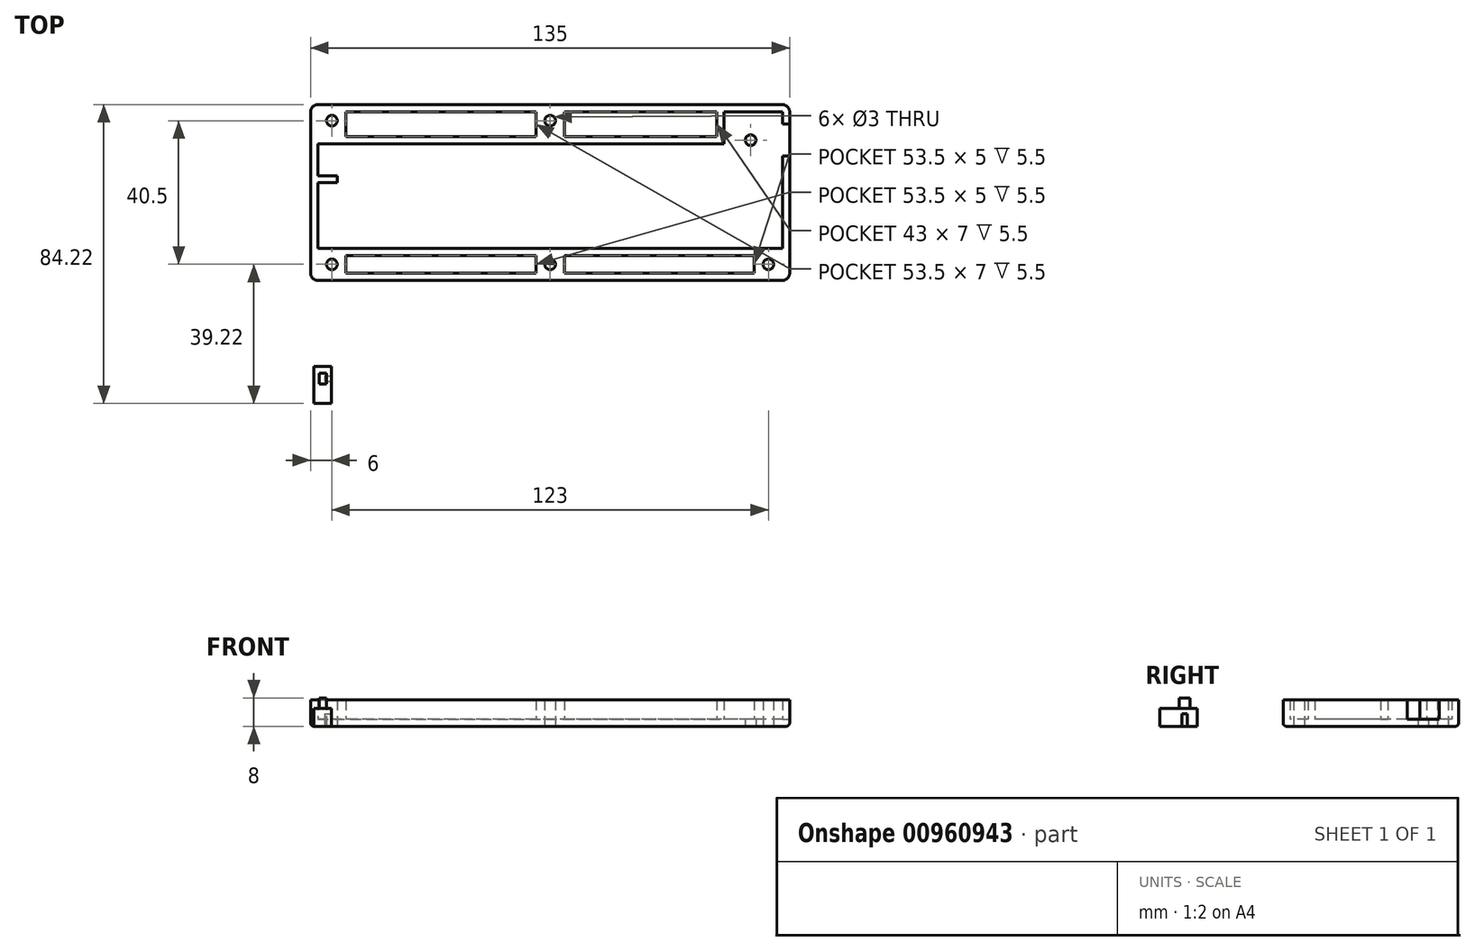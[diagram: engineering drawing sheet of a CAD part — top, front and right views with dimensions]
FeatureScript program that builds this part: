
annotation { "Feature Type Name" : "Feature", "Feature Type Description" : "" }
export const myFeature = defineFeature(function(context is Context, id is Id, definition is map)
    precondition{}
    {
        {
            var Q0;
            Q0=qCreatedBy(makeId("Top.planeOp"),FACE);
            var sketch = newSketch(context, id + "F0", { "sketchPlane" : qUnion([Q0])});
            skLineSegment(sketch, "E0.bottom", {"start": v(65.5, 19.25) * mm, "end": v(-65.5, 19.25) * mm});
            skLineSegment(sketch, "E0.top", {"start": v(65.5, -19.25) * mm, "end": v(-65.5, -19.25) * mm});
            skLineSegment(sketch, "E0.left", {"start": v(65.5, 19.25) * mm, "end": v(65.5, -19.25) * mm});
            skLineSegment(sketch, "E0.right", {"start": v(-65.5, 19.25) * mm, "end": v(-65.5, -19.25) * mm});
            skPoint(sketch, "E0.middle", {"position": v(0, 0) * mm});
            skPoint(sketch, "E1", {"position": v(49, 19.25) * mm});
            skPoint(sketch, "E2", {"position": v(-65.5, 10.25) * mm});
            skLineSegment(sketch, "E3", {"start": v(-65.5, 10.25) * mm, "end": v(49, 10.25) * mm});
            skLineSegment(sketch, "E4", {"start": v(49, 10.25) * mm, "end": v(49, 19.25) * mm});
            skPoint(sketch, "E5", {"position": v(-60, -19.25) * mm});
            skLineSegment(sketch, "E6", {"start": v(-60, -19.25) * mm, "end": v(-60, 10.25) * mm});
            skLineSegment(sketch, "E7.0", {"start": v(67.5, 21.25) * mm, "end": v(-67.5, 21.25) * mm});
            skLineSegment(sketch, "E7.1", {"start": v(67.5, 21.25) * mm, "end": v(67.5, -21.25) * mm});
            skLineSegment(sketch, "E7.2", {"start": v(67.5, -21.25) * mm, "end": v(-67.5, -21.25) * mm});
            skLineSegment(sketch, "E7.3", {"start": v(-67.5, 21.25) * mm, "end": v(-67.5, -21.25) * mm});
            skPoint(sketch, "E8", {"position": v(65.5, 15.75) * mm});
            skPoint(sketch, "E9", {"position": v(65.5, 6.75) * mm});
            skLineSegment(sketch, "E10.0", {"start": v(47, 12.25) * mm, "end": v(47, 19.25) * mm});
            skLineSegment(sketch, "E10.1", {"start": v(-65.5, 12.25) * mm, "end": v(47, 12.25) * mm});
            skPoint(sketch, "E11", {"position": v(-65.5, 1.25) * mm});
            skLineSegment(sketch, "E12", {"start": v(-65.5, 1.25) * mm, "end": v(-60, 1.25) * mm});
            skLineSegment(sketch, "E13.0", {"start": v(-65.5, -0.75) * mm, "end": v(-60, -0.75) * mm});
            skLineSegment(sketch, "E14", {"start": v(47, 19.25) * mm, "end": v(47, 21.25) * mm});
            skLineSegment(sketch, "E15", {"start": v(-65.5, 12.25) * mm, "end": v(-67.5, 12.25) * mm});
            skLineSegment(sketch, "E16", {"start": v(-65.5, 10.25) * mm, "end": v(-67.5, 10.25) * mm});
            skLineSegment(sketch, "E17", {"start": v(-65.5, 1.25) * mm, "end": v(-67.5, 1.25) * mm});
            skLineSegment(sketch, "E18", {"start": v(-65.5, -0.75) * mm, "end": v(-67.5, -0.75) * mm});
            skLineSegment(sketch, "E19", {"start": v(65.5, 15.75) * mm, "end": v(67.5, 15.75) * mm});
            skLineSegment(sketch, "E20", {"start": v(65.5, 6.75) * mm, "end": v(67.5, 6.75) * mm});
            skPoint(sketch, "E21", {"position": v(0, -19.25) * mm});
            skPoint(sketch, "E22", {"position": v(0, -4.25) * mm});
            skLineSegment(sketch, "E23.bottom", {"start": v(24, -13.25) * mm, "end": v(-24, -13.25) * mm});
            skLineSegment(sketch, "E23.top", {"start": v(24, 4.75) * mm, "end": v(-24, 4.75) * mm});
            skLineSegment(sketch, "E23.left", {"start": v(24, -13.25) * mm, "end": v(24, 4.75) * mm});
            skLineSegment(sketch, "E23.right", {"start": v(-24, -13.25) * mm, "end": v(-24, 4.75) * mm});
            skLineSegment(sketch, "E24.0", {"start": v(26, -15.25) * mm, "end": v(26, 6.75) * mm});
            skLineSegment(sketch, "E24.1", {"start": v(26, -15.25) * mm, "end": v(-26, -15.25) * mm});
            skLineSegment(sketch, "E24.2", {"start": v(-26, -15.25) * mm, "end": v(-26, 6.75) * mm});
            skLineSegment(sketch, "E24.3", {"start": v(26, 6.75) * mm, "end": v(-26, 6.75) * mm});
            skPoint(sketch, "E25", {"position": v(-67.5, -28.25) * mm});
            skLineSegment(sketch, "E26.bottom", {"start": v(-67.5, -28.25) * mm, "end": v(67.5, -28.25) * mm});
            skLineSegment(sketch, "E26.top", {"start": v(-67.5, -21.25) * mm, "end": v(67.5, -21.25) * mm});
            skLineSegment(sketch, "E26.left", {"start": v(-67.5, -28.25) * mm, "end": v(-67.5, -21.25) * mm});
            skLineSegment(sketch, "E26.right", {"start": v(67.5, -28.25) * mm, "end": v(67.5, -21.25) * mm});
            skPoint(sketch, "E27", {"position": v(-67.5, 16.75) * mm});
            skLineSegment(sketch, "E28", {"start": v(-67.5, 16.75) * mm, "end": v(47, 16.75) * mm, "construction": true});
            skPoint(sketch, "E29", {"position": v(-67.5, -23.75) * mm});
            skLineSegment(sketch, "E30", {"start": v(-67.5, -23.75) * mm, "end": v(67.5, -23.75) * mm, "construction": true});
            skPoint(sketch, "E31", {"position": v(-61.5, 16.75) * mm});
            skPoint(sketch, "E32", {"position": v(-61.5, -23.75) * mm});
            skPoint(sketch, "E33", {"position": v(61.5, -23.75) * mm});
            skPoint(sketch, "E34", {"position": v(0, -23.75) * mm});
            skPoint(sketch, "E35", {"position": v(0, 16.75) * mm});
            skPoint(sketch, "E36", {"position": v(65.5, 11.25) * mm});
            skPoint(sketch, "E37", {"position": v(56.5, 11.25) * mm});
            skCircle(sketch, "E38", {"center": v(56.5, 11.25) * mm, "radius": 1.5 * mm});
            skCircle(sketch, "E39", {"center": v(0, 16.75) * mm, "radius": 1.5 * mm});
            skCircle(sketch, "E40", {"center": v(-61.5, 16.75) * mm, "radius": 1.5 * mm});
            skCircle(sketch, "E41", {"center": v(-61.5, -23.75) * mm, "radius": 1.5 * mm});
            skCircle(sketch, "E42", {"center": v(0, -23.75) * mm, "radius": 1.5 * mm});
            skCircle(sketch, "E43", {"center": v(61.5, -23.75) * mm, "radius": 1.5 * mm});
            skPoint(sketch, "E44", {"position": v(-57.5, 21.25) * mm});
            skLineSegment(sketch, "E45", {"start": v(-57.5, 21.25) * mm, "end": v(-57.5, 12.25) * mm});
            skLineSegment(sketch, "E46.bottom", {"start": v(4, 12.25) * mm, "end": v(-4, 12.25) * mm});
            skLineSegment(sketch, "E46.top", {"start": v(4, 21.25) * mm, "end": v(-4, 21.25) * mm});
            skLineSegment(sketch, "E46.left", {"start": v(4, 12.25) * mm, "end": v(4, 21.25) * mm});
            skLineSegment(sketch, "E46.right", {"start": v(-4, 12.25) * mm, "end": v(-4, 21.25) * mm});
            skLineSegment(sketch, "E47", {"start": v(-57.5, -21.25) * mm, "end": v(-57.5, -28.25) * mm});
            skLineSegment(sketch, "E48.bottom", {"start": v(4, -19.25) * mm, "end": v(-4, -19.25) * mm});
            skLineSegment(sketch, "E48.top", {"start": v(4, -28.25) * mm, "end": v(-4, -28.25) * mm});
            skLineSegment(sketch, "E48.left", {"start": v(4, -19.25) * mm, "end": v(4, -28.25) * mm});
            skLineSegment(sketch, "E48.right", {"start": v(-4, -19.25) * mm, "end": v(-4, -28.25) * mm});
            skLineSegment(sketch, "E49", {"start": v(57.5, -28.25) * mm, "end": v(57.5, -19.25) * mm});
            skPoint(sketch, "E50", {"position": v(-67.5, -26.25) * mm});
            skLineSegment(sketch, "E51", {"start": v(-67.5, -26.25) * mm, "end": v(67.5, -26.25) * mm});
            skSolve(sketch);
        }
        {
            var Q0;
            {var subQ0=sQuery(id+"F0.wireOp",EDGE,"E4");Q0=makeQuery(id+"F0.imprint","IMPRINT",FACE,{"disambiguationData":[TD([[makeQuery(id+"F0.imprint","IMPRINT",EDGE,{"derivedFrom":subQ0}),-1.0]])]});}
            var Q1;
            {var subQ3=sQuery(id+"F0.wireOp",EDGE,"E12");Q1=makeQuery(id+"F0.imprint","IMPRINT",FACE,{"disambiguationData":[TD([[makeQuery(id+"F0.imprint","IMPRINT",EDGE,{"derivedFrom":subQ3}),1.0]])]});}
            var Q2;
            {var subQ5=sQuery(id+"F0.wireOp",EDGE,"E13.0");Q2=makeQuery(id+"F0.imprint","IMPRINT",FACE,{"disambiguationData":[TD([[makeQuery(id+"F0.imprint","IMPRINT",EDGE,{"derivedFrom":subQ5}),-1.0]])]});}
            var Q3;
            {var subQ2=sQuery(id+"F0.wireOp",EDGE,"E19");Q3=makeQuery(id+"F0.imprint","IMPRINT",FACE,{"disambiguationData":[TD([[makeQuery(id+"F0.imprint","IMPRINT",EDGE,{"derivedFrom":subQ2}),-1.0]])]});}
            var Q4;
            Q4=makeQuery(id+"F0.imprint","IMPRINT",FACE,{"disambiguationData":[TD([[makeQuery(id+"F0.imprint","IMPRINT",EDGE,{"derivedFrom":sQuery(id+"F0.wireOp",EDGE,"E23.bottom")}),1.0]])]});
            var Q5;
            {var subQ0=sQuery(id+"F0.wireOp",EDGE,"E46.right");var subQ1=sQuery(id+"F0.wireOp",EDGE,"E0.bottom");var subQ2=makeQuery(id+"F0.imprint","INTERSECT",VERTEX,{"derivedFrom":[subQ1,subQ0]});Q5=makeQuery(id+"F0.imprint","IMPRINT",FACE,{"disambiguationData":[TD([[makeQuery(id+"F0.imprint","IMPRINT",EDGE,{"disambiguationData":[TD([[subQ2,-1.0]])],"derivedFrom":subQ1}),1.0]])]});}
            var Q6;
            {var subQ0=sQuery(id+"F0.wireOp",EDGE,"E10.0");Q6=makeQuery(id+"F0.imprint","IMPRINT",FACE,{"disambiguationData":[TD([[makeQuery(id+"F0.imprint","IMPRINT",EDGE,{"derivedFrom":subQ0}),1.0]])]});}
            var Q7;
            {var subQ0=sQuery(id+"F0.wireOp",EDGE,"E49");var subQ1=sQuery(id+"F0.wireOp",EDGE,"E7.2");var subQ2=makeQuery(id+"F0.imprint","INTERSECT",VERTEX,{"derivedFrom":[subQ1,subQ0]});Q7=makeQuery(id+"F0.imprint","IMPRINT",FACE,{"disambiguationData":[TD([[makeQuery(id+"F0.imprint","IMPRINT",EDGE,{"disambiguationData":[TD([[subQ2,-1.0]])],"derivedFrom":subQ1}),1.0]])]});}
            var Q8;
            {var subQ0=sQuery(id+"F0.wireOp",EDGE,"E48.right");var subQ1=sQuery(id+"F0.wireOp",EDGE,"E7.2");var subQ2=makeQuery(id+"F0.imprint","INTERSECT",VERTEX,{"derivedFrom":[subQ1,subQ0]});Q8=makeQuery(id+"F0.imprint","IMPRINT",FACE,{"disambiguationData":[TD([[makeQuery(id+"F0.imprint","IMPRINT",EDGE,{"disambiguationData":[TD([[subQ2,-1.0]])],"derivedFrom":subQ1}),1.0]])]});}
            extrude(context, id + "F1", {"entities" : qUnion([Q0, Q1, Q2, Q3, Q4, Q5, Q6, Q7, Q8]), "depth" : 2 * mm, "offsetDistance" : 25 * mm});
        }
        {
            var Q0;
            {var subQ2=sQuery(id+"F0.wireOp",EDGE,"E4");Q0=makeQuery(id+"F0.imprint","IMPRINT",FACE,{"disambiguationData":[TD([[makeQuery(id+"F0.imprint","IMPRINT",EDGE,{"derivedFrom":subQ2}),1.0]])]});}
            var Q1;
            {var subQ2=sQuery(id+"F0.wireOp",EDGE,"E15");Q1=makeQuery(id+"F0.imprint","IMPRINT",FACE,{"disambiguationData":[TD([[makeQuery(id+"F0.imprint","IMPRINT",EDGE,{"derivedFrom":subQ2}),1.0]])]});}
            var Q2;
            {var subQ0=sQuery(id+"F0.wireOp",EDGE,"E16");Q2=makeQuery(id+"F0.imprint","IMPRINT",FACE,{"disambiguationData":[TD([[makeQuery(id+"F0.imprint","IMPRINT",EDGE,{"derivedFrom":subQ0}),1.0]])]});}
            var Q3;
            {var subQ2=sQuery(id+"F0.wireOp",EDGE,"E17");Q3=makeQuery(id+"F0.imprint","IMPRINT",FACE,{"disambiguationData":[TD([[makeQuery(id+"F0.imprint","IMPRINT",EDGE,{"derivedFrom":subQ2}),1.0]])]});}
            var Q4;
            {var subQ2=sQuery(id+"F0.wireOp",EDGE,"E12");Q4=makeQuery(id+"F0.imprint","IMPRINT",FACE,{"disambiguationData":[TD([[makeQuery(id+"F0.imprint","IMPRINT",EDGE,{"derivedFrom":subQ2}),-1.0]])]});}
            var Q5;
            {var subQ4=sQuery(id+"F0.wireOp",EDGE,"E7.2");Q5=makeQuery(id+"F0.imprint","IMPRINT",FACE,{"disambiguationData":[TD([[makeQuery(id+"F0.imprint","IMPRINT",EDGE,{"derivedFrom":subQ4}),-1.0]])]});}
            var Q6;
            {var subQ5=sQuery(id+"F0.wireOp",EDGE,"E14");Q6=makeQuery(id+"F0.imprint","IMPRINT",FACE,{"disambiguationData":[TD([[makeQuery(id+"F0.imprint","IMPRINT",EDGE,{"derivedFrom":subQ5}),-1.0]])]});}
            var Q7;
            {var subQ7=sQuery(id+"F0.wireOp",EDGE,"E18");Q7=makeQuery(id+"F0.imprint","IMPRINT",FACE,{"disambiguationData":[TD([[makeQuery(id+"F0.imprint","IMPRINT",EDGE,{"derivedFrom":subQ7}),1.0]])]});}
            var Q8;
            {var subQ0=sQuery(id+"F0.wireOp",EDGE,"E48.right");var subQ1=sQuery(id+"F0.wireOp",EDGE,"E0.top");var subQ2=makeQuery(id+"F0.imprint","INTERSECT",VERTEX,{"derivedFrom":[subQ1,subQ0]});Q8=makeQuery(id+"F0.imprint","IMPRINT",FACE,{"disambiguationData":[TD([[makeQuery(id+"F0.imprint","IMPRINT",EDGE,{"disambiguationData":[TD([[subQ2,1.0]])],"derivedFrom":subQ1}),1.0]])]});}
            var Q9;
            Q9=makeQuery(id+"F0.imprint","IMPRINT",FACE,{"disambiguationData":[TD([[makeQuery(id+"F0.imprint","IMPRINT",EDGE,{"derivedFrom":sQuery(id+"F0.wireOp",EDGE,"E42")}),-1.0]])]});
            var Q10;
            {var subQ0=sQuery(id+"F0.wireOp",EDGE,"E48.left");var subQ1=sQuery(id+"F0.wireOp",EDGE,"E0.top");var subQ2=makeQuery(id+"F0.imprint","INTERSECT",VERTEX,{"derivedFrom":[subQ1,subQ0]});Q10=makeQuery(id+"F0.imprint","IMPRINT",FACE,{"disambiguationData":[TD([[makeQuery(id+"F0.imprint","IMPRINT",EDGE,{"disambiguationData":[TD([[subQ2,1.0]])],"derivedFrom":subQ1}),1.0]])]});}
            var Q11;
            {var subQ0=sQuery(id+"F0.wireOp",EDGE,"E48.left");var subQ1=sQuery(id+"F0.wireOp",EDGE,"E26.bottom");var subQ2=makeQuery(id+"F0.imprint","INTERSECT",VERTEX,{"derivedFrom":[subQ1,subQ0]});Q11=makeQuery(id+"F0.imprint","IMPRINT",FACE,{"disambiguationData":[TD([[makeQuery(id+"F0.imprint","IMPRINT",EDGE,{"disambiguationData":[TD([[subQ2,1.0]])],"derivedFrom":subQ1}),1.0]])]});}
            var Q12;
            {var subQ0=sQuery(id+"F0.wireOp",EDGE,"E47");var subQ1=sQuery(id+"F0.wireOp",EDGE,"E26.bottom");var subQ2=makeQuery(id+"F0.imprint","INTERSECT",VERTEX,{"derivedFrom":[subQ1,subQ0]});Q12=makeQuery(id+"F0.imprint","IMPRINT",FACE,{"disambiguationData":[TD([[makeQuery(id+"F0.imprint","IMPRINT",EDGE,{"disambiguationData":[TD([[subQ2,-1.0]])],"derivedFrom":subQ1}),1.0]])]});}
            var Q13;
            {var subQ0=sQuery(id+"F0.wireOp",EDGE,"E48.left");var subQ1=sQuery(id+"F0.wireOp",EDGE,"E26.bottom");var subQ2=makeQuery(id+"F0.imprint","INTERSECT",VERTEX,{"derivedFrom":[subQ1,subQ0]});Q13=makeQuery(id+"F0.imprint","IMPRINT",FACE,{"disambiguationData":[TD([[makeQuery(id+"F0.imprint","IMPRINT",EDGE,{"disambiguationData":[TD([[subQ2,-1.0]])],"derivedFrom":subQ1}),1.0]])]});}
            var Q14;
            Q14=makeQuery(id+"F0.imprint","IMPRINT",FACE,{"disambiguationData":[TD([[makeQuery(id+"F0.imprint","IMPRINT",EDGE,{"derivedFrom":sQuery(id+"F0.wireOp",EDGE,"E41")}),-1.0]])]});
            var Q15;
            {var subQ0=sQuery(id+"F0.wireOp",EDGE,"E47");var subQ1=sQuery(id+"F0.wireOp",EDGE,"E26.bottom");var subQ2=makeQuery(id+"F0.imprint","INTERSECT",VERTEX,{"derivedFrom":[subQ1,subQ0]});Q15=makeQuery(id+"F0.imprint","IMPRINT",FACE,{"disambiguationData":[TD([[makeQuery(id+"F0.imprint","IMPRINT",EDGE,{"disambiguationData":[TD([[subQ2,1.0]])],"derivedFrom":subQ1}),1.0]])]});}
            var Q16;
            {var subQ5=sQuery(id+"F0.wireOp",EDGE,"E20");Q16=makeQuery(id+"F0.imprint","IMPRINT",FACE,{"disambiguationData":[TD([[makeQuery(id+"F0.imprint","IMPRINT",EDGE,{"derivedFrom":subQ5}),-1.0]])]});}
            var Q17;
            Q17=makeQuery(id+"F0.imprint","IMPRINT",FACE,{"disambiguationData":[TD([[makeQuery(id+"F0.imprint","IMPRINT",EDGE,{"derivedFrom":sQuery(id+"F0.wireOp",EDGE,"E43")}),-1.0]])]});
            var Q18;
            {var subQ0=sQuery(id+"F0.wireOp",EDGE,"E26.right");var subQ1=sQuery(id+"F0.wireOp",EDGE,"E26.bottom");var subQ2=makeQuery(id+"F0.imprint","INTERSECT",VERTEX,{"derivedFrom":[subQ1,subQ0]});Q18=makeQuery(id+"F0.imprint","IMPRINT",FACE,{"disambiguationData":[TD([[makeQuery(id+"F0.imprint","IMPRINT",EDGE,{"disambiguationData":[TD([[subQ2,1.0]])],"derivedFrom":subQ1}),1.0]])]});}
            var Q19;
            {var subQ0=sQuery(id+"F0.wireOp",EDGE,"E14");Q19=makeQuery(id+"F0.imprint","IMPRINT",FACE,{"disambiguationData":[TD([[makeQuery(id+"F0.imprint","IMPRINT",EDGE,{"derivedFrom":subQ0}),1.0]])]});}
            var Q20;
            {var subQ0=sQuery(id+"F0.wireOp",EDGE,"E46.right");var subQ1=sQuery(id+"F0.wireOp",EDGE,"E0.bottom");var subQ2=makeQuery(id+"F0.imprint","INTERSECT",VERTEX,{"derivedFrom":[subQ1,subQ0]});Q20=makeQuery(id+"F0.imprint","IMPRINT",FACE,{"disambiguationData":[TD([[makeQuery(id+"F0.imprint","IMPRINT",EDGE,{"disambiguationData":[TD([[subQ2,1.0]])],"derivedFrom":subQ1}),-1.0]])]});}
            var Q21;
            Q21=makeQuery(id+"F0.imprint","IMPRINT",FACE,{"disambiguationData":[TD([[makeQuery(id+"F0.imprint","IMPRINT",EDGE,{"derivedFrom":sQuery(id+"F0.wireOp",EDGE,"E39")}),-1.0]])]});
            var Q22;
            Q22=makeQuery(id+"F0.imprint","IMPRINT",FACE,{"disambiguationData":[TD([[makeQuery(id+"F0.imprint","IMPRINT",EDGE,{"derivedFrom":sQuery(id+"F0.wireOp",EDGE,"E40")}),-1.0]])]});
            var Q23;
            {var subQ0=sQuery(id+"F0.wireOp",EDGE,"E15");Q23=makeQuery(id+"F0.imprint","IMPRINT",FACE,{"disambiguationData":[TD([[makeQuery(id+"F0.imprint","IMPRINT",EDGE,{"derivedFrom":subQ0}),-1.0]])]});}
            var Q24;
            {var subQ0=sQuery(id+"F0.wireOp",EDGE,"E46.right");var subQ1=sQuery(id+"F0.wireOp",EDGE,"E0.bottom");var subQ2=makeQuery(id+"F0.imprint","INTERSECT",VERTEX,{"derivedFrom":[subQ1,subQ0]});Q24=makeQuery(id+"F0.imprint","IMPRINT",FACE,{"disambiguationData":[TD([[makeQuery(id+"F0.imprint","IMPRINT",EDGE,{"disambiguationData":[TD([[subQ2,-1.0]])],"derivedFrom":subQ1}),-1.0]])]});}
            extrude(context, id + "F2", {"entities" : qUnion([Q0, Q1, Q2, Q3, Q4, Q5, Q6, Q7, Q8, Q9, Q10, Q11, Q12, Q13, Q14, Q15, Q16, Q17, Q18, Q19, Q20, Q21, Q22, Q23, Q24]), "operationType" : NewBodyOperationType.ADD, "depth" : 7.5 * mm, "offsetDistance" : 25 * mm});
        }
        {
            var Q0;
            Q0=qCreatedBy(makeId("Top.planeOp"),FACE);
            var sketch = newSketch(context, id + "F3", { "sketchPlane" : qUnion([Q0])});
            skLineSegment(sketch, "E52.bottom", {"start": v(-66.58, -49.97) * mm, "end": v(-61.58, -49.97) * mm});
            skLineSegment(sketch, "E52.top", {"start": v(-66.58, -61.97) * mm, "end": v(-61.58, -61.97) * mm});
            skLineSegment(sketch, "E52.left", {"start": v(-66.58, -49.97) * mm, "end": v(-66.58, -61.97) * mm});
            skLineSegment(sketch, "E52.right", {"start": v(-61.58, -49.97) * mm, "end": v(-61.58, -61.97) * mm});
            skPoint(sketch, "E53", {"position": v(-61.58, -55.97) * mm});
            skLineSegment(sketch, "E54.left", {"start": v(-63.58, -55.22) * mm, "end": v(-63.58, -56.72) * mm});
            skLineSegment(sketch, "E55", {"start": v(-63.58, -56.72) * mm, "end": v(-61.58, -56.72) * mm});
            skLineSegment(sketch, "E56", {"start": v(-63.58, -55.22) * mm, "end": v(-61.58, -55.22) * mm});
            skSolve(sketch);
        }
        {
            var Q0;
            Q0=makeQuery(id+"F3.imprint","IMPRINT",FACE,{"disambiguationData":[TD([[makeQuery(id+"F3.imprint","IMPRINT",EDGE,{"derivedFrom":sQuery(id+"F3.wireOp",EDGE,"E52.bottom")}),-1.0]])]});
            var Q1;
            Q1=makeQuery(id+"F3.imprint","IMPRINT",FACE,{"disambiguationData":[TD([[makeQuery(id+"F3.imprint","IMPRINT",EDGE,{"derivedFrom":sQuery(id+"F3.wireOp",EDGE,"E54.left")}),1.0]])]});
            extrude(context, id + "F4", {"entities" : qUnion([Q0, Q1]), "depth" : 5 * mm, "offsetDistance" : 25 * mm});
        }
        {
            var Q0;
            Q0=makeQuery(id+"F3.imprint","IMPRINT",FACE,{"disambiguationData":[TD([[makeQuery(id+"F3.imprint","IMPRINT",EDGE,{"derivedFrom":sQuery(id+"F3.wireOp",EDGE,"E54.left")}),1.0]])]});
            extrude(context, id + "F5", {"entities" : qUnion([Q0]), "operationType" : NewBodyOperationType.REMOVE, "depth" : 3.5 * mm, "offsetDistance" : 25 * mm});
        }
        {
            var Q0;
            Q0=makeQuery(id+"F4.opExtrude","CAP_FACE",FACE,{"disambiguationData":[OSD([sQuery(id+"F3.wireOp",EDGE,"E52.bottom"),sQuery(id+"F3.wireOp",EDGE,"E52.top"),sQuery(id+"F3.wireOp",EDGE,"E52.left"),sQuery(id+"F3.wireOp",EDGE,"E52.right")])],"isStart":false});
            var sketch = newSketch(context, id + "F6", { "sketchPlane" : qUnion([Q0])});
            skLineSegment(sketch, "E57.bottom", {"start": v(-63.08, -57.47) * mm, "end": v(-65.08, -57.47) * mm});
            skLineSegment(sketch, "E57.top", {"start": v(-63.08, -54.47) * mm, "end": v(-65.08, -54.47) * mm});
            skLineSegment(sketch, "E57.left", {"start": v(-63.08, -57.47) * mm, "end": v(-63.08, -54.47) * mm});
            skLineSegment(sketch, "E57.right", {"start": v(-65.08, -57.47) * mm, "end": v(-65.08, -54.47) * mm});
            skPoint(sketch, "E57.middle", {"position": v(-64.08, -55.97) * mm});
            skPoint(sketch, "E57.middle.positionSnap0", {"position": v(-61.58, -55.97) * mm});
            skPoint(sketch, "E57.middle.positionSnap1", {"position": v(-64.08, -49.97) * mm});
            skPoint(sketch, "E57.centerSnap0", {"position": v(-61.58, -55.97) * mm});
            skPoint(sketch, "E57.centerSnap1", {"position": v(-64.08, -49.97) * mm});
            skSolve(sketch);
        }
        {
            var Q0;
            Q0=makeQuery(id+"F6.imprint","IMPRINT",FACE,{"disambiguationData":[TD([[makeQuery(id+"F6.imprint","IMPRINT",EDGE,{"derivedFrom":sQuery(id+"F6.wireOp",EDGE,"E57.bottom")}),-1.0]])]});
            extrude(context, id + "F7", {"entities" : qUnion([Q0]), "operationType" : NewBodyOperationType.ADD, "depth" : 3 * mm, "offsetDistance" : 25 * mm});
        }
        {
            var Q0;
            {var subQ0=sQuery(id+"F0.wireOp",EDGE,"E7.1");Q0=makeQuery(id+"F2.boolean.opBoolean","MERGE",EDGE,{"derivedFrom":[makeQuery(id+"F1.opExtrude","CAP_EDGE",EDGE,{"disambiguationData":[OSD([subQ0])],"isStart":true}),makeQuery(id+"F2.opExtrude","CAP_EDGE",EDGE,{"disambiguationData":[OSD([subQ0,sQuery(id+"F0.wireOp",EDGE,"E26.right")])],"isStart":true}),makeQuery(id+"F2.opExtrude","CAP_EDGE",EDGE,{"disambiguationData":[OSD([subQ0])],"isStart":true})]});}
            var Q1;
            Q1=makeQuery(id+"F2.opExtrude","CAP_EDGE",EDGE,{"disambiguationData":[OSD([sQuery(id+"F0.wireOp",EDGE,"E26.bottom")])],"isStart":true});
            var Q2;
            Q2=makeQuery(id+"F2.opExtrude","CAP_EDGE",EDGE,{"disambiguationData":[OSD([sQuery(id+"F0.wireOp",EDGE,"E7.0")])],"isStart":true});
            var Q3;
            Q3=makeQuery(id+"F2.opExtrude","CAP_EDGE",EDGE,{"disambiguationData":[OSD([sQuery(id+"F0.wireOp",EDGE,"E7.3"),sQuery(id+"F0.wireOp",EDGE,"E26.left")])],"isStart":true});
            fillet(context, id + "F8", {"entities" : qUnion([Q0, Q1, Q2, Q3]), "radius" : 1 * mm, "tangentPropagation" : true, "allowEdgeOverflow" : false});
        }
        {
            var Q0;
            Q0=makeQuery(id+"F2.opExtrude","SWEPT_EDGE",EDGE,{"disambiguationData":[OSD([sQuery(id+"F0.wireOp",EDGE,"E26.bottom"),sQuery(id+"F0.wireOp",EDGE,"E26.right")])]});
            var Q1;
            Q1=makeQuery(id+"F2.opExtrude","SWEPT_EDGE",EDGE,{"disambiguationData":[OSD([sQuery(id+"F0.wireOp",EDGE,"E7.0"),sQuery(id+"F0.wireOp",EDGE,"E7.1")])]});
            var Q2;
            Q2=makeQuery(id+"F2.opExtrude","SWEPT_EDGE",EDGE,{"disambiguationData":[OSD([sQuery(id+"F0.wireOp",EDGE,"E7.0"),sQuery(id+"F0.wireOp",EDGE,"E7.3")])]});
            var Q3;
            Q3=makeQuery(id+"F2.opExtrude","SWEPT_EDGE",EDGE,{"disambiguationData":[OSD([sQuery(id+"F0.wireOp",EDGE,"E26.bottom"),sQuery(id+"F0.wireOp",EDGE,"E26.left")])]});
            fillet(context, id + "F9", {"entities" : qUnion([Q0, Q1, Q2, Q3]), "radius" : 2 * mm, "tangentPropagation" : true, "allowEdgeOverflow" : false});
        }
        {
            var Q0;
            Q0=makeQuery(id+"F0.imprint","IMPRINT",FACE,{"disambiguationData":[TD([[makeQuery(id+"F0.imprint","IMPRINT",EDGE,{"derivedFrom":sQuery(id+"F0.wireOp",EDGE,"E23.bottom")}),-1.0]])]});
            extrude(context, id + "F10", {"entities" : qUnion([Q0]), "operationType" : NewBodyOperationType.ADD, "depth" : 2 * mm, "offsetDistance" : 25 * mm});
        }
        {
            var Q0;
            Q0=makeQuery(id+"F4.opExtrude","SWEPT_FACE",FACE,{"disambiguationData":[OSD([sQuery(id+"F3.wireOp",EDGE,"E52.top")])]});
            extrude(context, id + "F11", {"entities" : qUnion([Q0]), "operationType" : NewBodyOperationType.ADD, "depth" : 1 * mm, "offsetDistance" : 25 * mm});
        }
        {
            var Q0;
            Q0=makeQuery(id+"F4.opExtrude","SWEPT_FACE",FACE,{"disambiguationData":[OSD([sQuery(id+"F3.wireOp",EDGE,"E52.bottom")])]});
            extrude(context, id + "F12", {"entities" : qUnion([Q0]), "operationType" : NewBodyOperationType.REMOVE, "oppositeDirection" : true, "depth" : 2.5 * mm, "offsetDistance" : 25 * mm});
        }
    });
